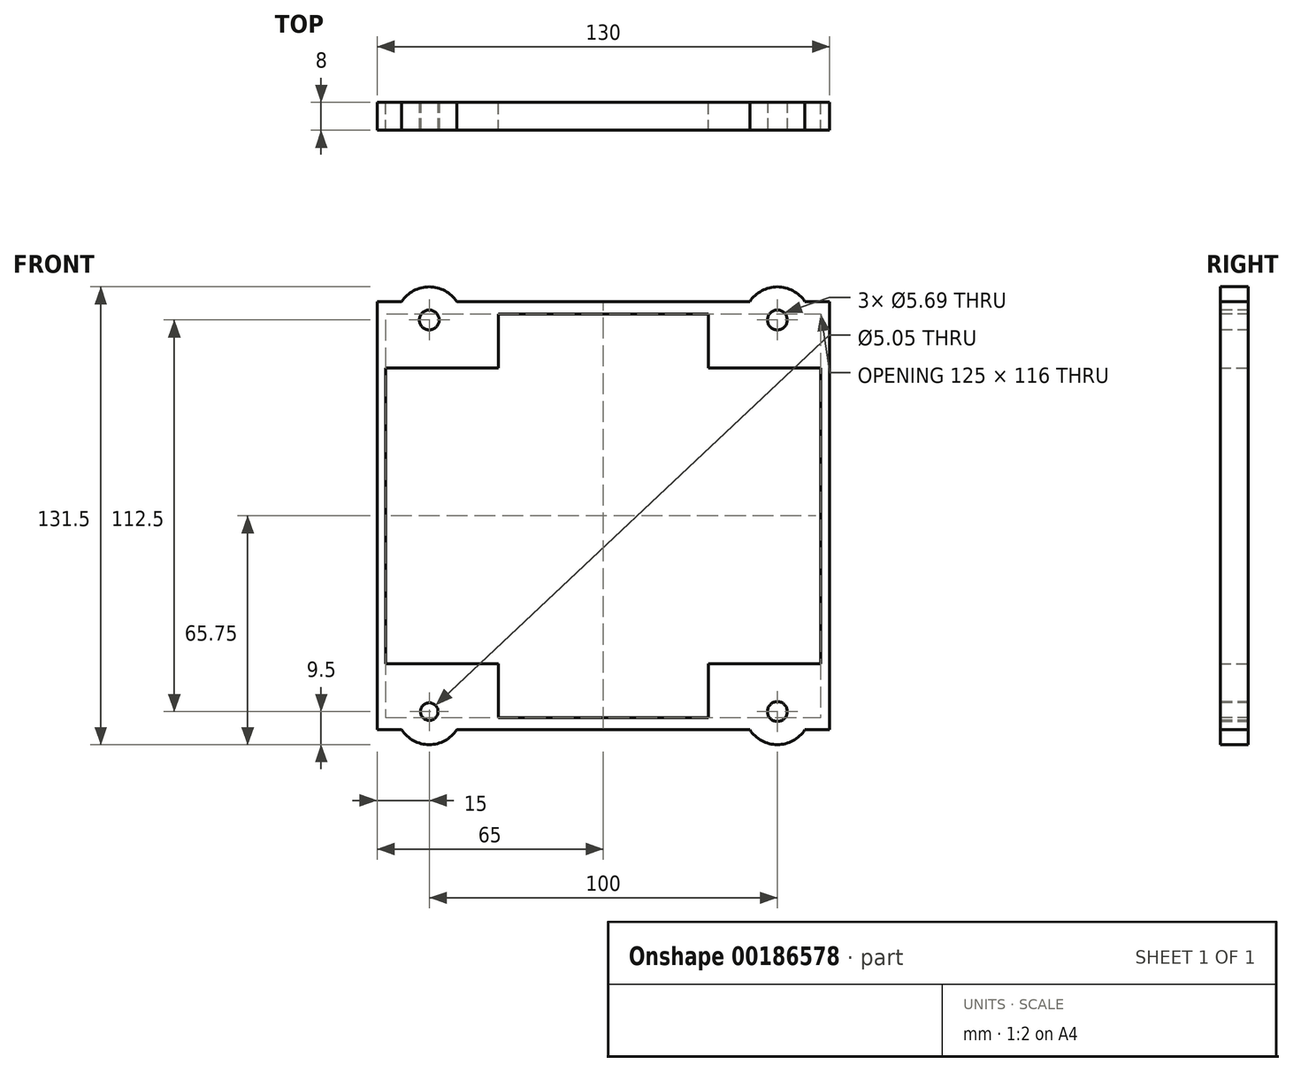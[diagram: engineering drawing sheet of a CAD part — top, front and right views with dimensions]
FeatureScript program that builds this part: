
annotation { "Feature Type Name" : "Feature", "Feature Type Description" : "" }
export const myFeature = defineFeature(function(context is Context, id is Id, definition is map)
    precondition{}
    {
        {
            var Q0;
            Q0=qCreatedBy(makeId("Front.planeOp"),FACE);
            var sketch = newSketch(context, id + "F0", { "sketchPlane" : qUnion([Q0])});
            skLineSegment(sketch, "E0.bottom", {"start": v(65, 61.5) * mm, "end": v(-65, 61.5) * mm});
            skLineSegment(sketch, "E0.top", {"start": v(65, -61.5) * mm, "end": v(-65, -61.5) * mm});
            skLineSegment(sketch, "E0.left", {"start": v(65, 61.5) * mm, "end": v(65, -61.5) * mm});
            skLineSegment(sketch, "E0.right", {"start": v(-65, 61.5) * mm, "end": v(-65, -61.5) * mm});
            skPoint(sketch, "E0.middle", {"position": v(0, 0) * mm});
            skLineSegment(sketch, "E1.bottom", {"start": v(62.5, 42.5) * mm, "end": v(-62.5, 42.5) * mm});
            skLineSegment(sketch, "E1.top", {"start": v(62.5, -42.5) * mm, "end": v(-62.5, -42.5) * mm});
            skLineSegment(sketch, "E1.left", {"start": v(62.5, 42.5) * mm, "end": v(62.5, -42.5) * mm});
            skLineSegment(sketch, "E1.right", {"start": v(-62.5, 42.5) * mm, "end": v(-62.5, -42.5) * mm});
            skSolve(sketch);
        }
        {
            var Q0;
            Q0 = qSketchRegion(id + "F0", true);
            extrude(context, id + "F1", {"entities" : qUnion([Q0]), "depth" : 8 * mm});
        }
        {
            var Q0;
            Q0=makeQuery(id+"F1.opExtrude","CAP_FACE",FACE,{"disambiguationData":[OSD([sQuery(id+"F0.wireOp",EDGE,"E0.bottom"),sQuery(id+"F0.wireOp",EDGE,"E0.top"),sQuery(id+"F0.wireOp",EDGE,"E0.left"),sQuery(id+"F0.wireOp",EDGE,"E0.right"),sQuery(id+"F0.wireOp",EDGE,"E1.bottom"),sQuery(id+"F0.wireOp",EDGE,"E1.top"),sQuery(id+"F0.wireOp",EDGE,"E1.left"),sQuery(id+"F0.wireOp",EDGE,"E1.right")])],"isStart":false});
            var sketch = newSketch(context, id + "F2", { "sketchPlane" : qUnion([Q0])});
            skCircle(sketch, "E2", {"center": v(-50, 56.25) * mm, "radius": 2.84 * mm});
            skCircle(sketch, "E3", {"center": v(50, 56.25) * mm, "radius": 2.84 * mm});
            skCircle(sketch, "E4", {"center": v(-50, -56.25) * mm, "radius": 2.52 * mm});
            skCircle(sketch, "E5", {"center": v(50, -56.25) * mm, "radius": 2.84 * mm});
            skSolve(sketch);
        }
        {
            var Q0;
            Q0 = qSketchRegion(id + "F2", true);
            extrude(context, id + "F3", {"entities" : qUnion([Q0]), "operationType" : NewBodyOperationType.REMOVE, "oppositeDirection" : true, "depth" : 25 * mm});
        }
        {
            var Q0;
            Q0=makeQuery(id+"F1.opExtrude","CAP_FACE",FACE,{"disambiguationData":[OSD([sQuery(id+"F0.wireOp",EDGE,"E0.bottom"),sQuery(id+"F0.wireOp",EDGE,"E0.top"),sQuery(id+"F0.wireOp",EDGE,"E0.left"),sQuery(id+"F0.wireOp",EDGE,"E0.right"),sQuery(id+"F0.wireOp",EDGE,"E1.bottom"),sQuery(id+"F0.wireOp",EDGE,"E1.top"),sQuery(id+"F0.wireOp",EDGE,"E1.left"),sQuery(id+"F0.wireOp",EDGE,"E1.right")])],"isStart":false});
            var sketch = newSketch(context, id + "F4", { "sketchPlane" : qUnion([Q0])});
            skLineSegment(sketch, "E6.bottom", {"start": v(-30.13, 58) * mm, "end": v(30.13, 58) * mm});
            skLineSegment(sketch, "E6.top", {"start": v(-30.13, -58) * mm, "end": v(30.13, -58) * mm});
            skLineSegment(sketch, "E6.left", {"start": v(-30.13, 58) * mm, "end": v(-30.13, -58) * mm});
            skLineSegment(sketch, "E6.right", {"start": v(30.13, 58) * mm, "end": v(30.13, -58) * mm});
            skPoint(sketch, "E6.middle", {"position": v(0, 0) * mm});
            skSolve(sketch);
        }
        {
            var Q0;
            Q0 = qSketchRegion(id + "F4", true);
            extrude(context, id + "F5", {"entities" : qUnion([Q0]), "operationType" : NewBodyOperationType.REMOVE, "oppositeDirection" : true, "depth" : 25 * mm});
        }
        {
            var Q0;
            Q0=makeQuery(id+"F1.opExtrude","CAP_FACE",FACE,{"disambiguationData":[OSD([sQuery(id+"F0.wireOp",EDGE,"E0.bottom"),sQuery(id+"F0.wireOp",EDGE,"E0.top"),sQuery(id+"F0.wireOp",EDGE,"E0.left"),sQuery(id+"F0.wireOp",EDGE,"E0.right"),sQuery(id+"F0.wireOp",EDGE,"E1.bottom"),sQuery(id+"F0.wireOp",EDGE,"E1.top"),sQuery(id+"F0.wireOp",EDGE,"E1.left"),sQuery(id+"F0.wireOp",EDGE,"E1.right")])],"isStart":true});
            var sketch = newSketch(context, id + "F6", { "sketchPlane" : qUnion([Q0])});
            skCircle(sketch, "E7.0", {"center": v(-50, 56.25) * mm, "radius": 2.84 * mm});
            skCircle(sketch, "E8.0", {"center": v(50, 56.25) * mm, "radius": 2.84 * mm});
            skCircle(sketch, "E9.0", {"center": v(50, -56.25) * mm, "radius": 2.52 * mm});
            skCircle(sketch, "E10.0", {"center": v(-50, -56.25) * mm, "radius": 2.84 * mm});
            skCircle(sketch, "E11", {"center": v(-50, 56.25) * mm, "radius": 9.5 * mm});
            skCircle(sketch, "E12.MirrorC", {"center": v(50, 56.25) * mm, "radius": 9.5 * mm});
            skCircle(sketch, "E13.MirrorC", {"center": v(-50, -56.25) * mm, "radius": 9.5 * mm});
            skCircle(sketch, "E14.MirrorC", {"center": v(50, -56.25) * mm, "radius": 9.5 * mm});
            skSolve(sketch);
        }
        {
            var Q0;
            Q0 = qSketchRegion(id + "F6", true);
            var Q1;
            Q1=makeQuery(id+"F1.opExtrude","CAP_FACE",FACE,{"disambiguationData":[OSD([sQuery(id+"F0.wireOp",EDGE,"E0.bottom"),sQuery(id+"F0.wireOp",EDGE,"E0.top"),sQuery(id+"F0.wireOp",EDGE,"E0.left"),sQuery(id+"F0.wireOp",EDGE,"E0.right"),sQuery(id+"F0.wireOp",EDGE,"E1.bottom"),sQuery(id+"F0.wireOp",EDGE,"E1.top"),sQuery(id+"F0.wireOp",EDGE,"E1.left"),sQuery(id+"F0.wireOp",EDGE,"E1.right")])],"isStart":false});
            extrude(context, id + "F7", {"entities" : qUnion([Q0]), "operationType" : NewBodyOperationType.ADD, "endBound" : BoundingType.UP_TO_SURFACE, "oppositeDirection" : true, "endBoundEntityFace" : qUnion([Q1]), "depth" : 25 * mm});
        }
    });
